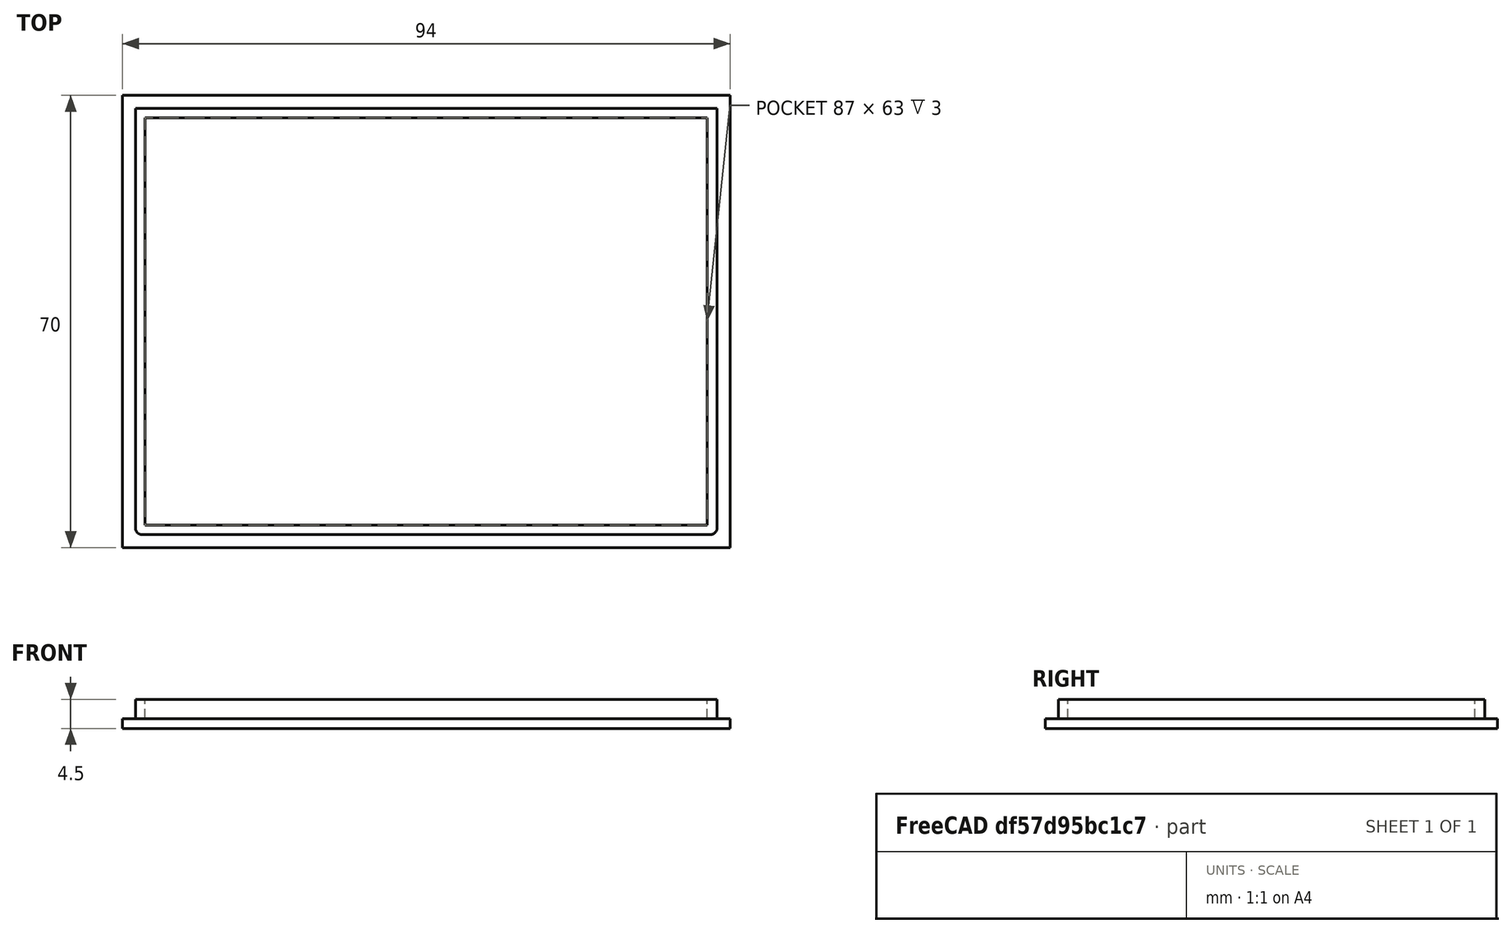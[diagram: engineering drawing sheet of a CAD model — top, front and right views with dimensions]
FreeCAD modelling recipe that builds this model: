
FCSTD DOCUMENT  (FreeCAD 0.19R22846 (Git))
Label: rainsensor deckel
License: All rights reserved
LicenseURL: http://en.wikipedia.org/wiki/All_rights_reserved
objects: Part::Fillet×3, Part::Box×2, Part::Thickness×1, Part::MultiFuse×1, Part::Refine×1
note: 8 computed .brp shape members not serialized (recipe doc carries the construction recipe); baked Part::Feature solids carry a one-line shape summary decoded from their .brp

FEATURE [Part::Box] Box  label="Würfel"
  AttacherType = Attacher::AttachEngine3D
  Height = 1.5
  Length = 94
  Width = 70
FEATURE [Part::Box] Box001  label="Würfel001"
  AttacherType = Attacher::AttachEngine3D
  Height = 4.5
  Length = 90
  Placement = pos=(2,2,0) rot=(0,0.894427,0.447214;0rad)
  Width = 66
FEATURE [Part::Thickness] Thickness
  Faces = -> Box001 [Face6]
  Intersection = false
  Join = 0
  Mode = 0
  SelfIntersection = false
  Value = -1.5
FEATURE [Part::Fillet] Fillet
  Base = -> Thickness
  Edges = 2 edges r=1: [Edge1,Edge7]
FEATURE [Part::Fillet] Fillet002
  Base = -> Fillet
  Edges = 2 edges r=1: [Edge4,Edge17]
FEATURE [Part::Fillet] Fillet001
  Base = -> Thickness
  Edges = 2 edges r=1.5: [Edge1,Edge7]
FEATURE [Part::MultiFuse] Fusion
  Shapes = -> [Fillet002,Fillet001,Box]
FEATURE [Part::Refine] Fusion001
  Source = -> Fusion
